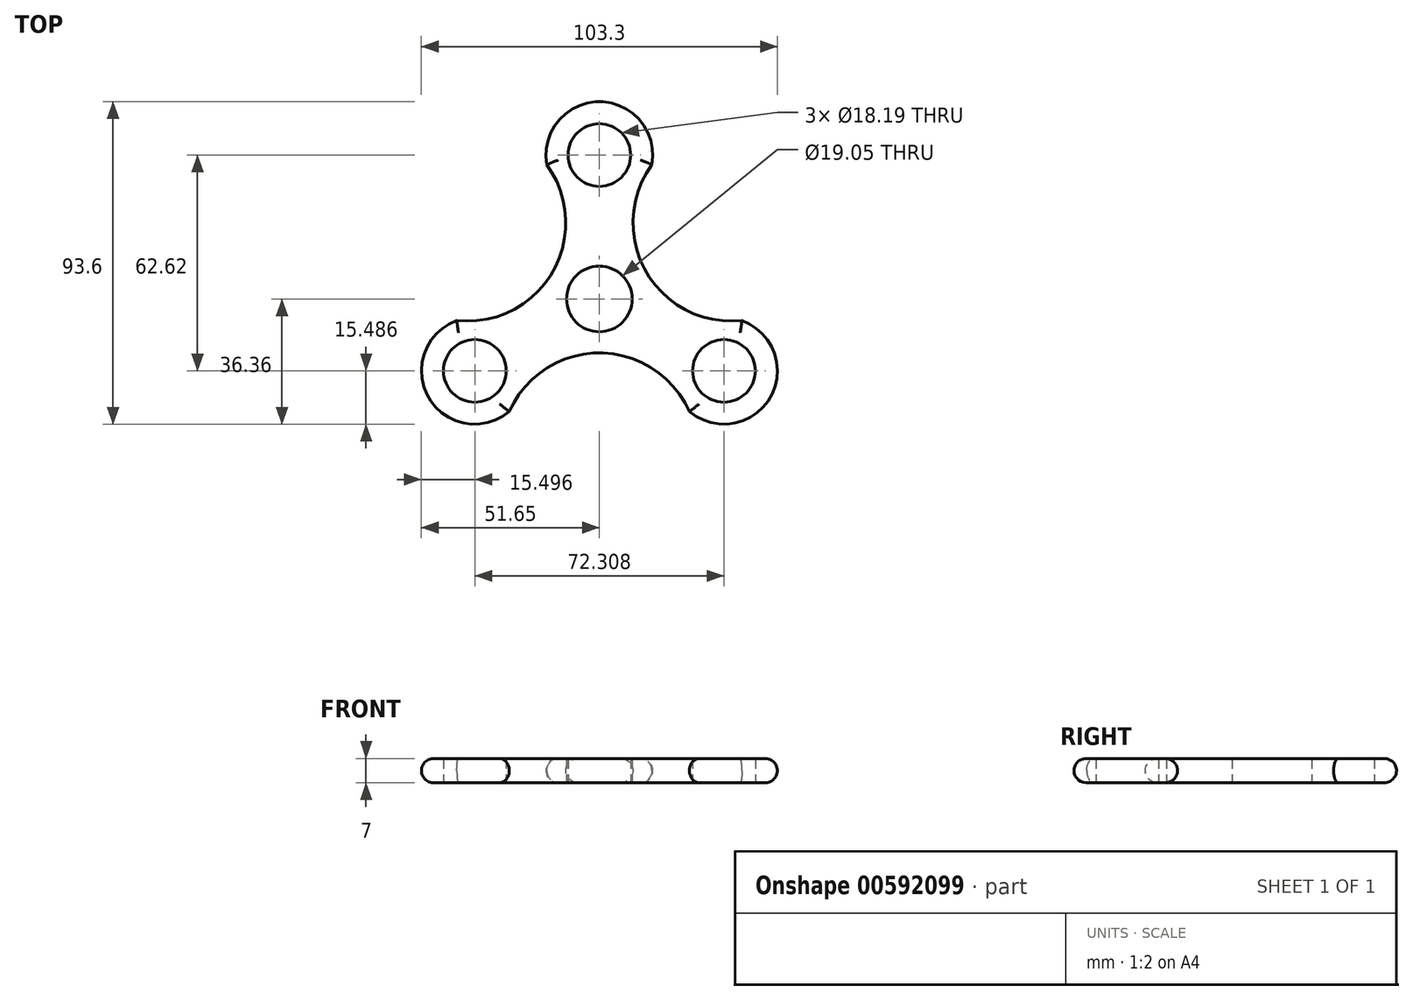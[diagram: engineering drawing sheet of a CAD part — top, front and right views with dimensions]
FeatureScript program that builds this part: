
annotation { "Feature Type Name" : "Feature", "Feature Type Description" : "" }
export const myFeature = defineFeature(function(context is Context, id is Id, definition is map)
    precondition{}
    {
        {
            var Q0;
            Q0=qCreatedBy(makeId("Top.planeOp"),FACE);
            var sketch = newSketch(context, id + "F0", { "sketchPlane" : qUnion([Q0])});
            skArc(sketch, "E0", {"start": v(15.24, 38.97) * mm, "mid": v(0, 57.24) * mm, "end": v(-15.24, 38.97) * mm});
            skArc(sketch, "E1.1.0", {"start": v(-41.37, -6.29) * mm, "mid": v(-49.57, -28.62) * mm, "end": v(-26.13, -32.68) * mm});
            skArc(sketch, "E1.2.0", {"start": v(26.13, -32.69) * mm, "mid": v(49.57, -28.62) * mm, "end": v(41.37, -6.29) * mm});
            skPoint(sketch, "E1.center", {"position": v(0, 0) * mm});
            skCircle(sketch, "E2", {"center": v(0, 41.75) * mm, "radius": 9.1 * mm});
            skCircle(sketch, "E3.1.0", {"center": v(-36.15, -20.87) * mm, "radius": 9.1 * mm});
            skCircle(sketch, "E3.2.0", {"center": v(36.15, -20.87) * mm, "radius": 9.1 * mm});
            skCircle(sketch, "E4", {"center": v(0, 0) * mm, "radius": 9.53 * mm});
            skPoint(sketch, "E5.MirrorCS.end.orphan", {"position": v(-14.3, 13.88) * mm});
            skPoint(sketch, "E5.MirrorCS.start.orphan", {"position": v(-12.4, 32.45) * mm});
            skPoint(sketch, "E6.start.orphan", {"position": v(12.4, 32.45) * mm});
            skPoint(sketch, "E7.trimOffspring.end.orphan", {"position": v(14.3, 13.88) * mm});
            skArc(sketch, "E8", {"start": v(15.24, 38.97) * mm, "mid": v(13.57, 7.84) * mm, "end": v(41.37, -6.29) * mm});
            skArc(sketch, "E9.1.0", {"start": v(-41.37, -6.29) * mm, "mid": v(-13.57, 7.83) * mm, "end": v(-15.24, 38.97) * mm});
            skArc(sketch, "E9.2.0", {"start": v(26.13, -32.69) * mm, "mid": v(0, -15.67) * mm, "end": v(-26.13, -32.68) * mm});
            skSolve(sketch);
        }
        {
            var Q0;
            Q0=makeQuery(id+"F0.imprint","IMPRINT",FACE,{"disambiguationData":[TD([[makeQuery(id+"F0.imprint","IMPRINT",EDGE,{"derivedFrom":sQuery(id+"F0.wireOp",EDGE,"E0")}),1.0]])]});
            extrude(context, id + "F1", {"entities" : qUnion([Q0]), "depth" : 7 * mm, "offsetDistance" : 25 * mm});
        }
        {
            var Q0;
            Q0=makeQuery(id+"F1.opExtrude","CAP_EDGE",EDGE,{"disambiguationData":[OSD([sQuery(id+"F0.wireOp",EDGE,"E9.2.0")])],"isStart":false});
            var Q1;
            Q1=makeQuery(id+"F1.opExtrude","CAP_EDGE",EDGE,{"disambiguationData":[OSD([sQuery(id+"F0.wireOp",EDGE,"E8")])],"isStart":true});
            var Q2;
            Q2=makeQuery(id+"F1.opExtrude","CAP_EDGE",EDGE,{"disambiguationData":[OSD([sQuery(id+"F0.wireOp",EDGE,"E9.1.0")])],"isStart":true});
            var Q3;
            Q3=makeQuery(id+"F1.opExtrude","CAP_EDGE",EDGE,{"disambiguationData":[OSD([sQuery(id+"F0.wireOp",EDGE,"E1.2.0")])],"isStart":true});
            var Q4;
            Q4=makeQuery(id+"F1.opExtrude","CAP_EDGE",EDGE,{"disambiguationData":[OSD([sQuery(id+"F0.wireOp",EDGE,"E9.2.0")])],"isStart":true});
            var Q5;
            Q5=makeQuery(id+"F1.opExtrude","CAP_EDGE",EDGE,{"disambiguationData":[OSD([sQuery(id+"F0.wireOp",EDGE,"E1.1.0")])],"isStart":true});
            var Q6;
            Q6=makeQuery(id+"F1.opExtrude","CAP_EDGE",EDGE,{"disambiguationData":[OSD([sQuery(id+"F0.wireOp",EDGE,"E0")])],"isStart":true});
            var Q7;
            Q7=makeQuery(id+"F1.opExtrude","CAP_EDGE",EDGE,{"disambiguationData":[OSD([sQuery(id+"F0.wireOp",EDGE,"E8")])],"isStart":false});
            var Q8;
            Q8=makeQuery(id+"F1.opExtrude","CAP_EDGE",EDGE,{"disambiguationData":[OSD([sQuery(id+"F0.wireOp",EDGE,"E9.1.0")])],"isStart":false});
            var Q9;
            Q9=makeQuery(id+"F1.opExtrude","CAP_EDGE",EDGE,{"disambiguationData":[OSD([sQuery(id+"F0.wireOp",EDGE,"E1.1.0")])],"isStart":false});
            var Q10;
            Q10=makeQuery(id+"F1.opExtrude","CAP_EDGE",EDGE,{"disambiguationData":[OSD([sQuery(id+"F0.wireOp",EDGE,"E0")])],"isStart":false});
            var Q11;
            Q11=makeQuery(id+"F1.opExtrude","CAP_EDGE",EDGE,{"disambiguationData":[OSD([sQuery(id+"F0.wireOp",EDGE,"E1.2.0")])],"isStart":false});
            fillet(context, id + "F2", {"entities" : qUnion([Q0, Q1, Q2, Q3, Q4, Q5, Q6, Q7, Q8, Q9, Q10, Q11]), "radius" : 3.5 * mm, "tangentPropagation" : true, "allowEdgeOverflow" : false});
        }
    });
